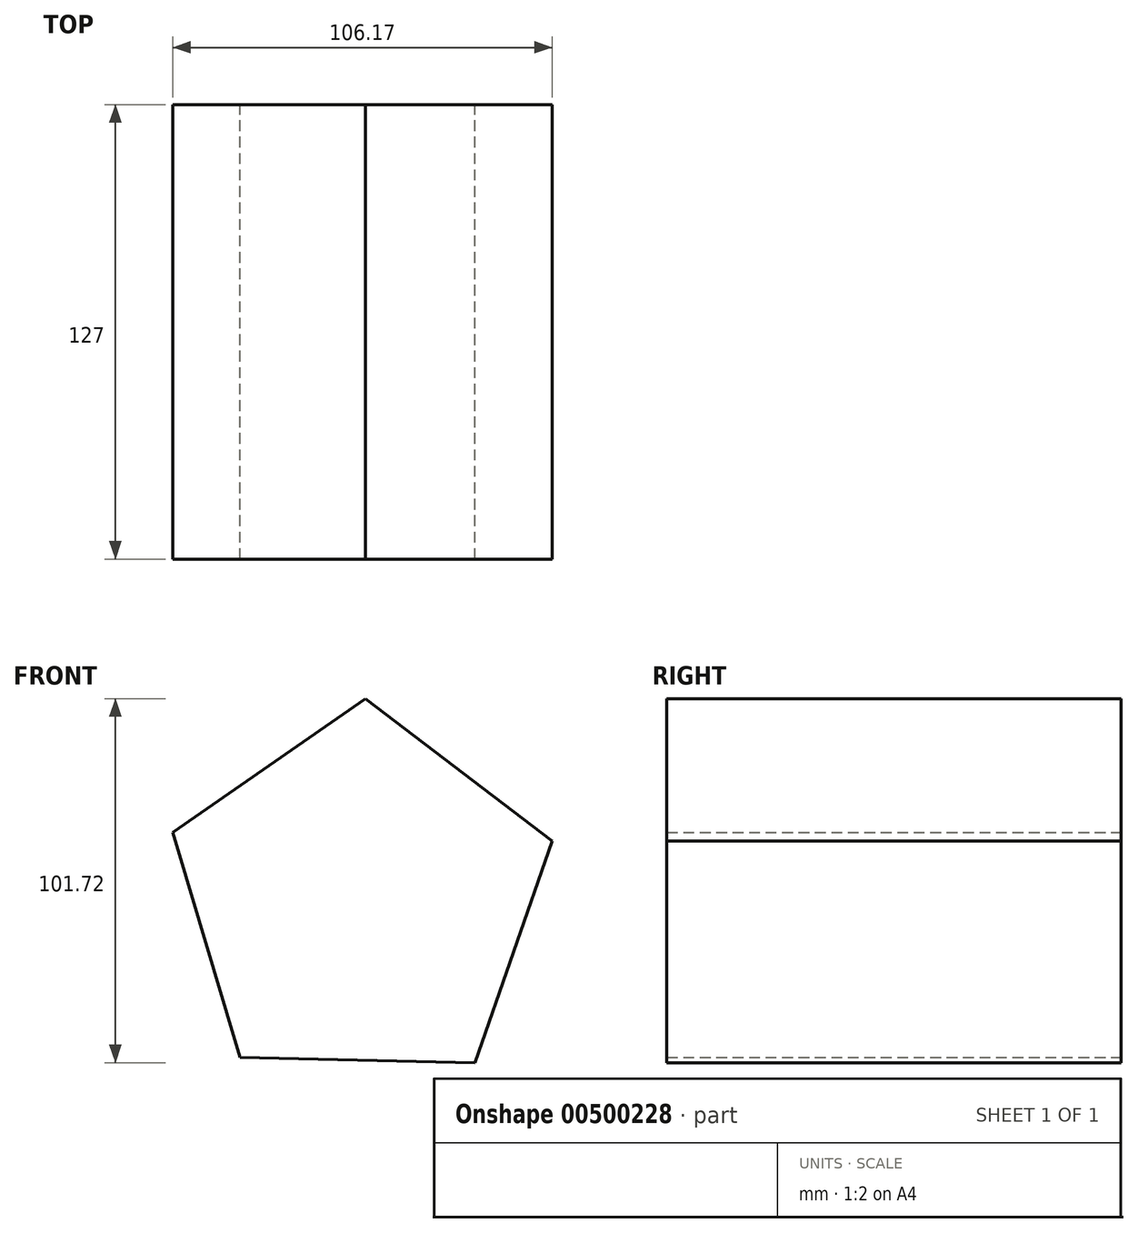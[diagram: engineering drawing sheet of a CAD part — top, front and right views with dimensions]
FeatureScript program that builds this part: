
annotation { "Feature Type Name" : "Feature", "Feature Type Description" : "" }
export const myFeature = defineFeature(function(context is Context, id is Id, definition is map)
    precondition{}
    {
        {
            var Q0;
            Q0=qCreatedBy(makeId("Front.planeOp"),FACE);
            var sketch = newSketch(context, id + "F0", { "sketchPlane" : qUnion([Q0])});
            skCircle(sketch, "E0.cCircle", {"center": v(0, 0) * mm, "radius": 55.83 * mm, "construction": true});
            skLineSegment(sketch, "E0.0", {"start": v(31.77, -45.9) * mm, "end": v(-33.84, -44.4) * mm});
            skLineSegment(sketch, "E0.1", {"start": v(-33.84, -44.4) * mm, "end": v(-52.69, 18.47) * mm});
            skLineSegment(sketch, "E0.2", {"start": v(-52.69, 18.47) * mm, "end": v(1.28, 55.81) * mm});
            skLineSegment(sketch, "E0.3", {"start": v(1.28, 55.81) * mm, "end": v(53.48, 16.03) * mm});
            skLineSegment(sketch, "E0.4", {"start": v(53.48, 16.03) * mm, "end": v(31.77, -45.9) * mm});
            skSolve(sketch);
        }
        {
            var Q0;
            Q0 = qSketchRegion(id + "F0", true);
            extrude(context, id + "F1", {"entities" : qUnion([Q0]), "depth" : 127 * mm});
        }
    });
